# Revit family: Domotics-DomesticRanges-GEWISS-SYSTEM_POWER-SOCKET-OUTLET_FRA
name_source: partatom
category: Apparecchi elettrici
revit_build: Autodesk Revit 2016 (Build: 20161004_0715(x64)
units: mm (PartAtom-declared; Revit-internal decimal feet)

## family parameters
Condiviso = Sì
Host = Superficie
Mantenere orientamento annotazione = Sì
Punto di calcolo locali = Sì
Quota connettore circolare = Usa diametro
Taglio con vuoti quando caricato = Sì
Tipo di parte = Normale

## types (5) — shared parameters
Carico apparente = 0 VA
Catalogue = DOMOTICS
Catalogue Range = SYSTEM - DOMESTIC RANGE
Description. = France
Electrocod = 0131
For plug pins = Ã˜ 4 / 4.8 mm
IDF = babc6fc7-54f3-4548-b33f-10fc7bc1d9fd
IDT = 59e86ad9-7750-4562-ad2a-436f4590d886
Immagine tipo = GW21207.jpg
N. poli = 1
No. SYSTEM modules = 2
Produttore = GEWISS S.p.A.
Prospetto di default = 1219 mm
SEO = Socket outlet
Standard = French
Standard: = French
TIPO_ = System Prese Fra_GENERICO : GW21207 Presa 2P+T 16A standard Francese nero
TXT ELETTRICO = 16
Technical sheet = https://www.gewiss.com
URL = https://www.gewiss.com
Version file RFA = 19.4
Volt = 230 V
Voltage = 250 V ac
Voltage: = 250 V ac

## per-type parameters (varying)
| type | Colour | Description: | Descrizione | EAN code | Modello | Type | Type: |
| GW20206 - 16A 2P french socket outlet white | White | 2P - 16A | 16A 2P FRENCH SOCKET OUTLET SY/WT | 8011564000582 | GW20206 |  |  |
| GW20207 - 16A 2P+E french socket outlet white | White | 2P+E - 16A | 16A 2P+E FRENCH SOCKET OUTLET SY/WT | 8011564000599 | GW20207 |  |  |
| GW20312 - 2P+E 16A french red socket | Red | 2P+E - 16A | 2P+E 16A FRENCH RED SOCKET | 8011564099364 | GW20312 | For allocated lines | For allocated lines |
| GW21207 - 16A 2P+E french socket outlet black | Black | 2P+E - 16A | 16A 2P+E FRENCH SOCKET OUTLET SY/BK | 8011564128491 | GW21207 |  |  |
| GW21206 - 16A 2P french socket outlet black | Black | 2P - 16A | 16A 2P FRENCH SOCKET OUTLET SY/BK | 8011564128484 | GW21206 |  |  |

## geometry (parser evidence)
native form markers: Sweep x2
no freeform markers — native parametric forms only
